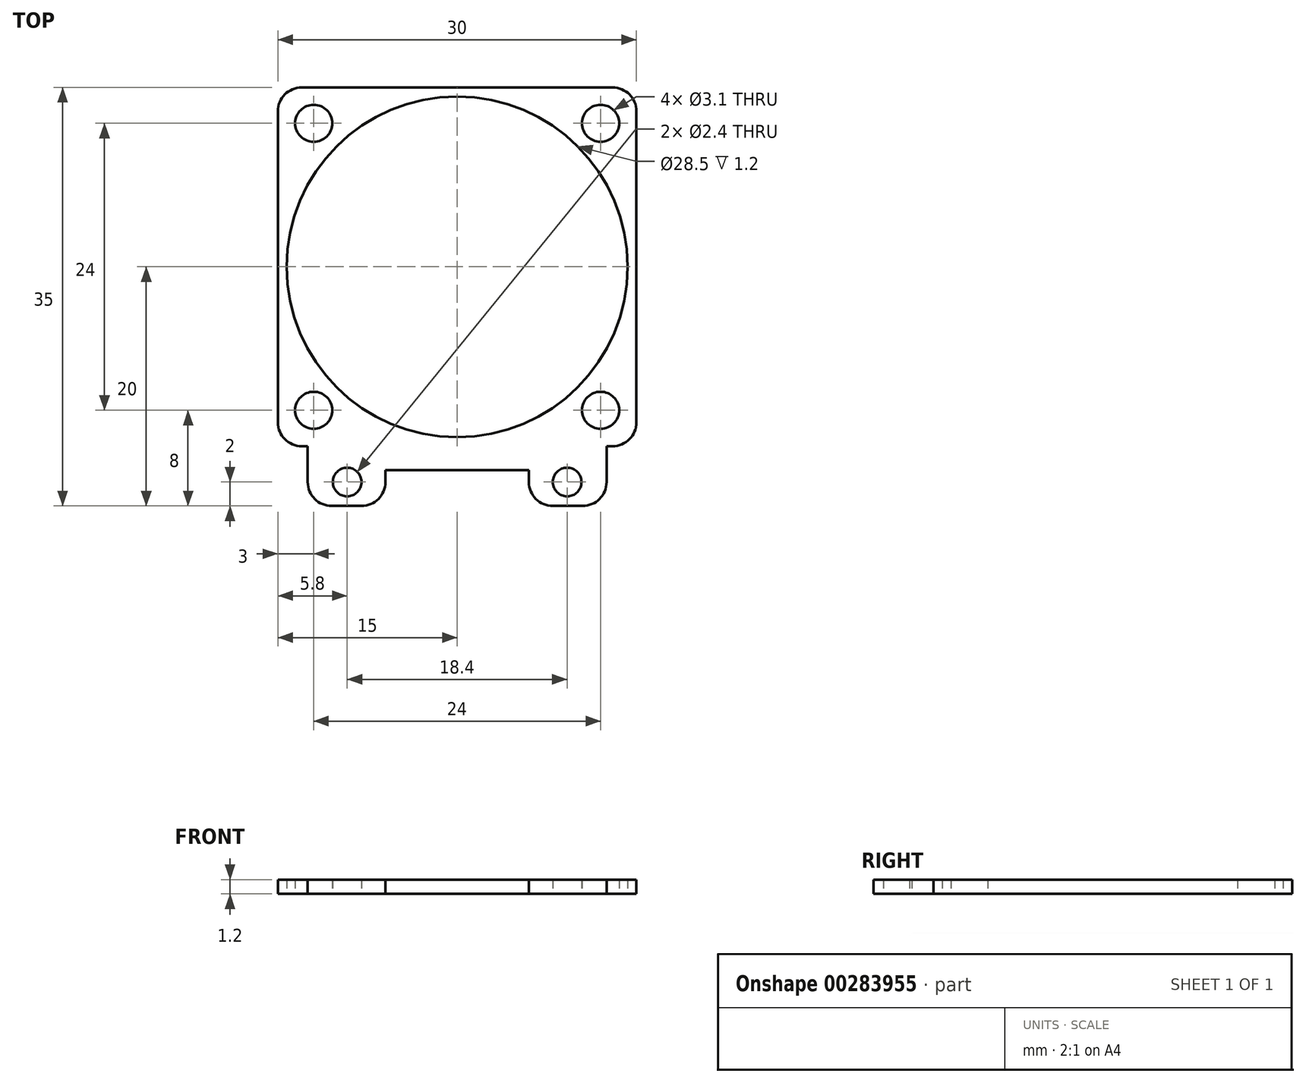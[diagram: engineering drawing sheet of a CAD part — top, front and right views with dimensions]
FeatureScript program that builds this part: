
annotation { "Feature Type Name" : "Feature", "Feature Type Description" : "" }
export const myFeature = defineFeature(function(context is Context, id is Id, definition is map)
    precondition{}
    {
        {
            var Q0;
            Q0=qCreatedBy(makeId("Top.planeOp"),FACE);
            var sketch = newSketch(context, id + "F0", { "sketchPlane" : qUnion([Q0])});
            skLineSegment(sketch, "E0.bottom", {"start": v(15, -15) * mm, "end": v(-15, -15) * mm});
            skLineSegment(sketch, "E0.top", {"start": v(15, 15) * mm, "end": v(-15, 15) * mm});
            skLineSegment(sketch, "E0.left", {"start": v(15, -15) * mm, "end": v(15, 15) * mm});
            skLineSegment(sketch, "E0.right", {"start": v(-15, -15) * mm, "end": v(-15, 15) * mm});
            skPoint(sketch, "E0.middle", {"position": v(0, 0) * mm});
            skLineSegment(sketch, "E1.bottom", {"start": v(12, -12) * mm, "end": v(-12, -12) * mm, "construction": true});
            skLineSegment(sketch, "E1.top", {"start": v(12, 12) * mm, "end": v(-12, 12) * mm, "construction": true});
            skLineSegment(sketch, "E1.left", {"start": v(12, -12) * mm, "end": v(12, 12) * mm, "construction": true});
            skLineSegment(sketch, "E1.right", {"start": v(-12, -12) * mm, "end": v(-12, 12) * mm, "construction": true});
            skCircle(sketch, "E2", {"center": v(-12, 12) * mm, "radius": 1.55 * mm});
            skCircle(sketch, "E3", {"center": v(12, 12) * mm, "radius": 1.55 * mm});
            skCircle(sketch, "E4", {"center": v(12, -12) * mm, "radius": 1.55 * mm});
            skCircle(sketch, "E5", {"center": v(-12, -12) * mm, "radius": 1.55 * mm});
            skLineSegment(sketch, "E6", {"start": v(-14.96, -20) * mm, "end": v(-6, -20) * mm, "construction": true});
            skLineSegment(sketch, "E7.bottom", {"start": v(-15, -15) * mm, "end": v(15, -15) * mm});
            skLineSegment(sketch, "E7.top", {"start": v(-6, -17) * mm, "end": v(6, -17) * mm});
            skLineSegment(sketch, "E8.bottom", {"start": v(-12.5, -15) * mm, "end": v(12.5, -15) * mm});
            skLineSegment(sketch, "E8.top", {"start": v(-12.5, -20) * mm, "end": v(-6, -20) * mm});
            skLineSegment(sketch, "E8.left", {"start": v(-12.5, -15) * mm, "end": v(-12.5, -20) * mm});
            skLineSegment(sketch, "E8.right", {"start": v(12.5, -15) * mm, "end": v(12.5, -20) * mm});
            skLineSegment(sketch, "E9.bottom", {"start": v(-6, -15) * mm, "end": v(6, -15) * mm});
            skLineSegment(sketch, "E9.left", {"start": v(-6, -15) * mm, "end": v(-6, -20) * mm});
            skLineSegment(sketch, "E9.right", {"start": v(6, -15) * mm, "end": v(6, -20) * mm});
            skPoint(sketch, "E7.right.end.orphan", {"position": v(15, -17) * mm});
            skLineSegment(sketch, "E10.trimOffspring", {"start": v(6, -20) * mm, "end": v(15.77, -20) * mm, "construction": true});
            skLineSegment(sketch, "E11.trimOffspring", {"start": v(6, -20) * mm, "end": v(12.5, -20) * mm});
            skLineSegment(sketch, "E12", {"start": v(-13.8, -18) * mm, "end": v(14.7, -18) * mm, "construction": true});
            skLineSegment(sketch, "E13", {"start": v(-9.2, -15) * mm, "end": v(-9.2, -21.94) * mm, "construction": true});
            skLineSegment(sketch, "E14", {"start": v(9.2, -15) * mm, "end": v(9.2, -21.94) * mm, "construction": true});
            skCircle(sketch, "E15", {"center": v(-9.2, -18) * mm, "radius": 1.2 * mm});
            skCircle(sketch, "E16", {"center": v(9.2, -18) * mm, "radius": 1.2 * mm});
            skCircle(sketch, "E17", {"center": v(0, 0) * mm, "radius": 14.25 * mm});
            skSolve(sketch);
        }
        {
            var Q0;
            Q0=makeQuery(id+"F0.imprint","IMPRINT",FACE,{"disambiguationData":[TD([[makeQuery(id+"F0.imprint","IMPRINT",EDGE,{"derivedFrom":sQuery(id+"F0.wireOp",EDGE,"E0.top")}),1.0]])]});
            var Q1;
            {var subQ4=sQuery(id+"F0.wireOp",EDGE,"E8.top");Q1=makeQuery(id+"F0.imprint","IMPRINT",FACE,{"disambiguationData":[TD([[makeQuery(id+"F0.imprint","IMPRINT",EDGE,{"derivedFrom":subQ4}),1.0]])]});}
            var Q2;
            {var subQ0=sQuery(id+"F0.wireOp",EDGE,"E7.top");Q2=makeQuery(id+"F0.imprint","IMPRINT",FACE,{"disambiguationData":[TD([[makeQuery(id+"F0.imprint","IMPRINT",EDGE,{"derivedFrom":subQ0}),1.0]])]});}
            var Q3;
            {var subQ5=sQuery(id+"F0.wireOp",EDGE,"E8.right");Q3=makeQuery(id+"F0.imprint","IMPRINT",FACE,{"disambiguationData":[TD([[makeQuery(id+"F0.imprint","IMPRINT",EDGE,{"derivedFrom":subQ5}),-1.0]])]});}
            extrude(context, id + "F1", {"entities" : qUnion([Q0, Q1, Q2, Q3]), "depth" : 1.2 * mm, "offsetDistance" : 25 * mm});
        }
        {
            var Q0;
            Q0=makeQuery(id+"F1.opExtrude","SWEPT_EDGE",EDGE,{"disambiguationData":[OSD([sQuery(id+"F0.wireOp",EDGE,"E0.left"),sQuery(id+"F0.wireOp",EDGE,"E7.bottom")])]});
            var Q1;
            Q1=makeQuery(id+"F1.opExtrude","SWEPT_EDGE",EDGE,{"disambiguationData":[OSD([sQuery(id+"F0.wireOp",EDGE,"E0.right"),sQuery(id+"F0.wireOp",EDGE,"E7.bottom")])]});
            var Q2;
            Q2=makeQuery(id+"F1.opExtrude","SWEPT_EDGE",EDGE,{"disambiguationData":[OSD([sQuery(id+"F0.wireOp",EDGE,"E0.top"),sQuery(id+"F0.wireOp",EDGE,"E0.right")])]});
            var Q3;
            Q3=makeQuery(id+"F1.opExtrude","SWEPT_EDGE",EDGE,{"disambiguationData":[OSD([sQuery(id+"F0.wireOp",EDGE,"E0.top"),sQuery(id+"F0.wireOp",EDGE,"E0.left")])]});
            var Q4;
            {var subQ0=sQuery(id+"F0.wireOp",EDGE,"E8.left");var subQ1=sQuery(id+"F0.wireOp",EDGE,"E8.top");Q4=makeQuery(id+"Fwv7ShQSevM5gkZ_1.boolean.opBoolean","MERGE",EDGE,{"derivedFrom":[makeQuery(id+"F1.opExtrude","SWEPT_EDGE",EDGE,{"disambiguationData":[OSD([subQ1,subQ0])]}),makeQuery(id+"Fwv7ShQSevM5gkZ_1.opExtrude","SWEPT_EDGE",EDGE,{"disambiguationData":[OSD([subQ1,subQ0])]})]});}
            var Q5;
            {var subQ0=sQuery(id+"F0.wireOp",EDGE,"E9.left");var subQ1=sQuery(id+"F0.wireOp",EDGE,"E8.top");Q5=makeQuery(id+"Fwv7ShQSevM5gkZ_1.boolean.opBoolean","MERGE",EDGE,{"derivedFrom":[makeQuery(id+"F1.opExtrude","SWEPT_EDGE",EDGE,{"disambiguationData":[OSD([subQ1,subQ0])]}),makeQuery(id+"Fwv7ShQSevM5gkZ_1.opExtrude","SWEPT_EDGE",EDGE,{"disambiguationData":[OSD([subQ1,subQ0])]})]});}
            var Q6;
            {var subQ0=sQuery(id+"F0.wireOp",EDGE,"E11.trimOffspring");var subQ1=sQuery(id+"F0.wireOp",EDGE,"E9.right");Q6=makeQuery(id+"Fwv7ShQSevM5gkZ_1.boolean.opBoolean","MERGE",EDGE,{"derivedFrom":[makeQuery(id+"F1.opExtrude","SWEPT_EDGE",EDGE,{"disambiguationData":[OSD([subQ1,subQ0])]}),makeQuery(id+"Fwv7ShQSevM5gkZ_1.opExtrude","SWEPT_EDGE",EDGE,{"disambiguationData":[OSD([subQ1,subQ0])]})]});}
            var Q7;
            {var subQ0=sQuery(id+"F0.wireOp",EDGE,"E11.trimOffspring");var subQ1=sQuery(id+"F0.wireOp",EDGE,"E8.right");Q7=makeQuery(id+"Fwv7ShQSevM5gkZ_1.boolean.opBoolean","MERGE",EDGE,{"derivedFrom":[makeQuery(id+"F1.opExtrude","SWEPT_EDGE",EDGE,{"disambiguationData":[OSD([subQ1,subQ0])]}),makeQuery(id+"Fwv7ShQSevM5gkZ_1.opExtrude","SWEPT_EDGE",EDGE,{"disambiguationData":[OSD([subQ1,subQ0])]})]});}
            var Q8;
            Q8=makeQuery(id+"Fwv7ShQSevM5gkZ_1.opExtrude","SWEPT_EDGE",EDGE,{"disambiguationData":[OSD([sQuery(id+"F0.wireOp",EDGE,"E7.bottom"),sQuery(id+"F0.wireOp",EDGE,"E8.bottom"),sQuery(id+"F0.wireOp",EDGE,"E8.right")])]});
            var Q9;
            Q9=makeQuery(id+"Fwv7ShQSevM5gkZ_1.opExtrude","SWEPT_EDGE",EDGE,{"disambiguationData":[OSD([sQuery(id+"F0.wireOp",EDGE,"E7.bottom"),sQuery(id+"F0.wireOp",EDGE,"E8.bottom"),sQuery(id+"F0.wireOp",EDGE,"E8.left")])]});
            fillet(context, id + "F2", {"entities" : qUnion([Q0, Q1, Q2, Q3, Q4, Q5, Q6, Q7, Q8, Q9]), "radius" : 2 * mm, "tangentPropagation" : true, "allowEdgeOverflow" : false});
        }
    });
